# Revit family: ВУТ_ВУЕ міні_Eng
name_source: partatom
category: Mechanical Equipment
units: mm (PartAtom-declared; Revit-internal decimal feet)

## family parameters
Always vertical = Yes
Classification = None
Cut with Voids When Loaded = No
Part Type = Normal
Room Calculation Point = No
Round Connector Dimension = Use Diameter
Shared = No
Work Plane-Based = No

## types (8) — shared parameters
00_20_Manufacturer = Vents
00_20_Name = Air handling units with heat recovery
Amperage = 1 A
B = 300 mm
Casing Material = Steel, galvanized
D = 125 mm  [stored 0.410105 ft]
Diameter = 125 mm  [stored 0.410105 ft]
Frequency = 50 Hz
H = 443 mm  [stored 1.45341 ft]
L = 713 mm
Load Classification = HVAC
Maintenance zone material = <By Category>
Manufacturer = Vents
Number of Fase = 1
URL = https://ventilation-system.com
Voltage = 230 V
Width = 300 mm
b = 280 mm  [stored 0.918635 ft]
zero-valued in all types: Default Elevation

## per-type parameters (varying)
| type | Apparent Load | Control | El box big on the side | El box big on top | Filter | H1 | Height | L1 | Length | Maximum Air Flow | Power | Sound pressure level at 3 m distance | Terminal box on the side | Terminal box top | Vent channels goriz | Vent channels vertical |
| VUE 250 V mini A1 | 138 VA | Yes | No | No | G4 | 490 mm  [stored 1.60761 ft] | 933 mm  [stored 3.06102 ft] | 0 mm  [stored 0 ft] | 0 mm  [stored 0 ft] | 260.0 m³/h | 126 W | 28...47 dBA | Yes | No | No | Yes |
| VUE 250 H mini A1 | 138 VA | No | No | No | G4 | 43 mm  [stored 0.141076 ft] | 486 mm  [stored 1.59449 ft] | 810 mm | 810 mm | 260.0 m³/h | 126 W | 28...47 dBA | No | Yes | Yes | No |
| VUE 300 V2 mini EC A14 | 299 VA | No | Yes | No | G4, F8 | 490 mm  [stored 1.60761 ft] | 933 mm  [stored 3.06102 ft] | 0 mm  [stored 0 ft] | 0 mm  [stored 0 ft] | 300.0 m³/h | 165 W | 33 dBA | No | No | No | Yes |
| VUE 300 H2 mini EC A14 | 299 VA | No | No | Yes | G4, F8 | 43 mm  [stored 0.141076 ft] | 486 mm  [stored 1.59449 ft] | 810 mm | 810 mm | 300.0 m³/h | 165 W | 33  dBA | No | No | Yes | No |
| VUT 250 V mini A1 | 138 VA | Yes | No | No | G4 | 490 mm  [stored 1.60761 ft] | 933 mm  [stored 3.06102 ft] | 0 mm  [stored 0 ft] | 0 mm  [stored 0 ft] | 260.0 m³/h | 126 W | 28...47 dBA | Yes | No | No | Yes |
| VUT 250 H mini A1 | 138 VA | No | No | No | G4 | 43 mm  [stored 0.141076 ft] | 486 mm  [stored 1.59449 ft] | 810 mm | 810 mm | 260.0 m³/h | 126 W | 28...47 dBA | No | Yes | Yes | No |
| VUT 300 V2 mini EC A14 | 299 VA | No | Yes | No | G4, F8 | 490 mm  [stored 1.60761 ft] | 933 mm  [stored 3.06102 ft] | 0 mm  [stored 0 ft] | 0 mm  [stored 0 ft] | 300.0 m³/h | 165 W | 33 dBA | No | No | No | Yes |
| VUT 300 H2 mini EC A14 | 299 VA | No | No | Yes | G4, F8 | 43 mm  [stored 0.141076 ft] | 486 mm  [stored 1.59449 ft] | 810 mm | 810 mm | 300.0 m³/h | 165 W | 33  dBA | No | No | Yes | No |

note: column(s) folded — value = type name in every type: 00_20_Type

note: [stored X ft] marks values corroborated as IEEE doubles in the binary element streams (Revit-internal decimal feet)
